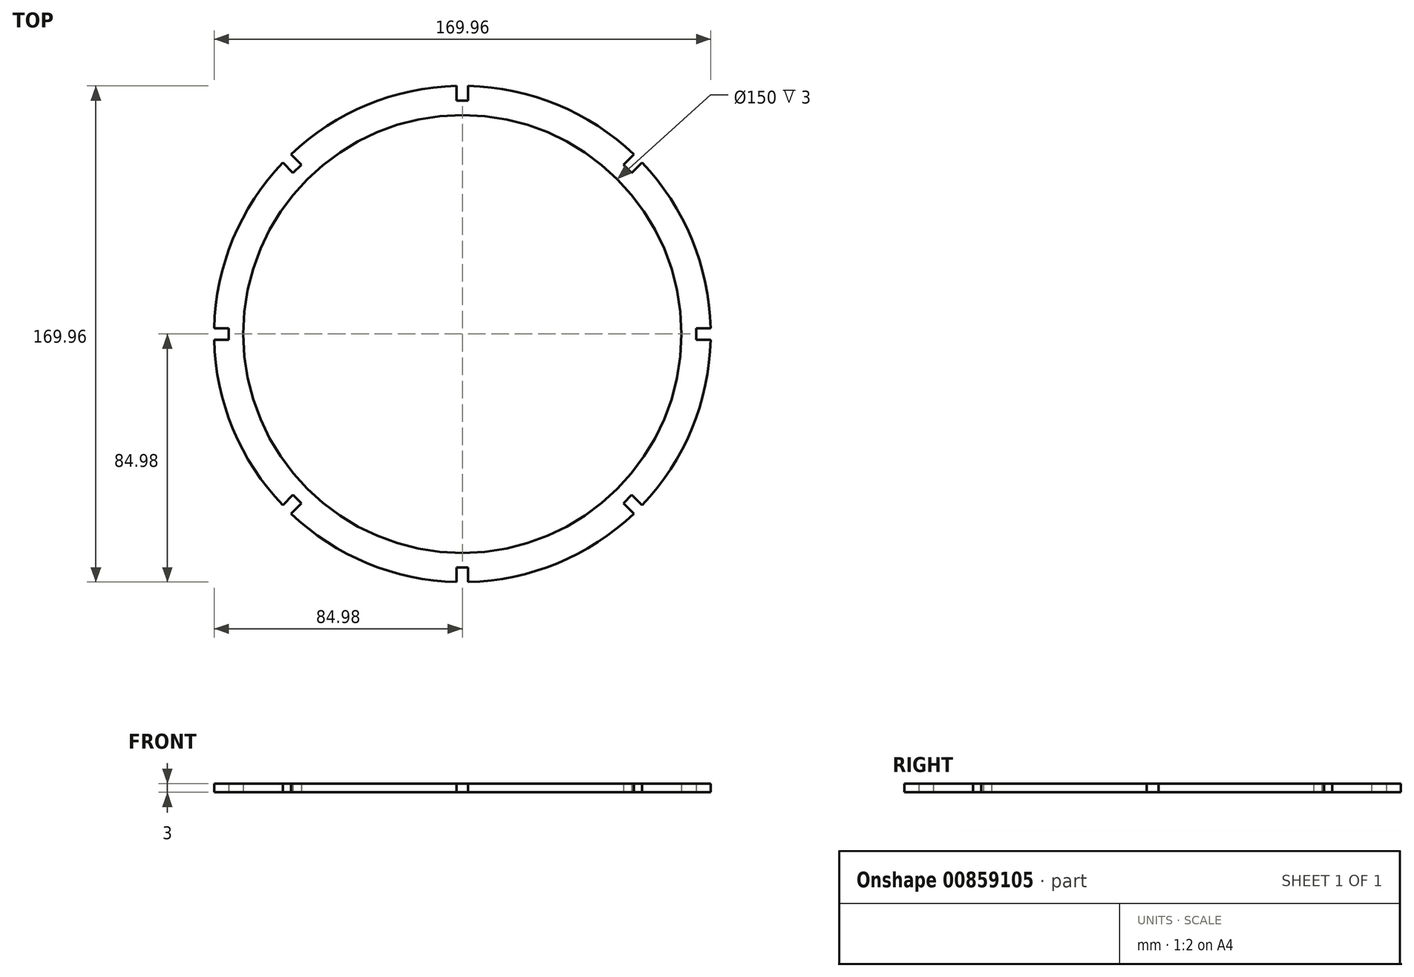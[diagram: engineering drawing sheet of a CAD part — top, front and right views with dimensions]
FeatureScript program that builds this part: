
annotation { "Feature Type Name" : "Feature", "Feature Type Description" : "" }
export const myFeature = defineFeature(function(context is Context, id is Id, definition is map)
    precondition{}
    {
        {
            var Q0;
            Q0=qCreatedBy(makeId("Top.planeOp"),FACE);
            var sketch = newSketch(context, id + "F0", { "sketchPlane" : qUnion([Q0])});
            skCircle(sketch, "E0", {"center": v(0, 0) * mm, "radius": 85 * mm});
            skCircle(sketch, "E1", {"center": v(0, 0) * mm, "radius": 75 * mm});
            skLineSegment(sketch, "E2", {"start": v(0, -79.98) * mm, "end": v(-2, -79.98) * mm});
            skLineSegment(sketch, "E3", {"start": v(-2, -79.98) * mm, "end": v(-2, -84.98) * mm});
            skLineSegment(sketch, "E4", {"start": v(-2, -84.98) * mm, "end": v(-2, -79.98) * mm});
            skLineSegment(sketch, "E5", {"start": v(0, -79.98) * mm, "end": v(2, -79.98) * mm});
            skLineSegment(sketch, "E6", {"start": v(2, -79.98) * mm, "end": v(2, -84.98) * mm});
            skLineSegment(sketch, "E7.1.0", {"start": v(55.14, -57.97) * mm, "end": v(58.67, -61.5) * mm});
            skLineSegment(sketch, "E7.1.1", {"start": v(56.55, -56.55) * mm, "end": v(55.14, -57.97) * mm});
            skLineSegment(sketch, "E7.1.2", {"start": v(56.55, -56.55) * mm, "end": v(57.97, -55.14) * mm});
            skLineSegment(sketch, "E7.1.3", {"start": v(57.97, -55.14) * mm, "end": v(61.5, -58.67) * mm});
            skLineSegment(sketch, "E7.2.0", {"start": v(79.98, -2) * mm, "end": v(84.98, -2) * mm});
            skLineSegment(sketch, "E7.2.1", {"start": v(79.98, 0) * mm, "end": v(79.98, -2) * mm});
            skLineSegment(sketch, "E7.2.2", {"start": v(79.98, 0) * mm, "end": v(79.98, 2) * mm});
            skLineSegment(sketch, "E7.2.3", {"start": v(79.98, 2) * mm, "end": v(84.98, 2) * mm});
            skLineSegment(sketch, "E7.3.0", {"start": v(57.97, 55.14) * mm, "end": v(61.5, 58.67) * mm});
            skLineSegment(sketch, "E7.3.1", {"start": v(56.55, 56.55) * mm, "end": v(57.97, 55.14) * mm});
            skLineSegment(sketch, "E7.3.2", {"start": v(56.55, 56.55) * mm, "end": v(55.14, 57.97) * mm});
            skLineSegment(sketch, "E7.3.3", {"start": v(55.14, 57.97) * mm, "end": v(58.67, 61.5) * mm});
            skLineSegment(sketch, "E7.4.0", {"start": v(2, 79.98) * mm, "end": v(2, 84.98) * mm});
            skLineSegment(sketch, "E7.4.1", {"start": v(0, 79.98) * mm, "end": v(2, 79.98) * mm});
            skLineSegment(sketch, "E7.4.2", {"start": v(0, 79.98) * mm, "end": v(-2, 79.98) * mm});
            skLineSegment(sketch, "E7.4.3", {"start": v(-2, 79.98) * mm, "end": v(-2, 84.98) * mm});
            skLineSegment(sketch, "E7.5.0", {"start": v(-55.14, 57.97) * mm, "end": v(-58.67, 61.5) * mm});
            skLineSegment(sketch, "E7.5.1", {"start": v(-56.55, 56.55) * mm, "end": v(-55.14, 57.97) * mm});
            skLineSegment(sketch, "E7.5.2", {"start": v(-56.55, 56.55) * mm, "end": v(-57.97, 55.14) * mm});
            skLineSegment(sketch, "E7.5.3", {"start": v(-57.97, 55.14) * mm, "end": v(-61.5, 58.67) * mm});
            skLineSegment(sketch, "E7.6.0", {"start": v(-79.98, 2) * mm, "end": v(-84.98, 2) * mm});
            skLineSegment(sketch, "E7.6.1", {"start": v(-79.98, 0) * mm, "end": v(-79.98, 2) * mm});
            skLineSegment(sketch, "E7.6.2", {"start": v(-79.98, 0) * mm, "end": v(-79.98, -2) * mm});
            skLineSegment(sketch, "E7.6.3", {"start": v(-79.98, -2) * mm, "end": v(-84.98, -2) * mm});
            skLineSegment(sketch, "E7.7.0", {"start": v(-57.97, -55.14) * mm, "end": v(-61.5, -58.67) * mm});
            skLineSegment(sketch, "E7.7.1", {"start": v(-56.55, -56.55) * mm, "end": v(-57.97, -55.14) * mm});
            skLineSegment(sketch, "E7.7.2", {"start": v(-56.55, -56.55) * mm, "end": v(-55.14, -57.97) * mm});
            skLineSegment(sketch, "E7.7.3", {"start": v(-55.14, -57.97) * mm, "end": v(-58.67, -61.5) * mm});
            skSolve(sketch);
        }
        {
            var Q0;
            Q0=makeQuery(id+"F0.imprint","IMPRINT",FACE,{"disambiguationData":[TD([[makeQuery(id+"F0.imprint","IMPRINT",EDGE,{"derivedFrom":sQuery(id+"F0.wireOp",EDGE,"E1")}),-1.0]])]});
            extrude(context, id + "F1", {"entities" : qUnion([Q0]), "depth" : 3 * mm, "offsetDistance" : 25 * mm});
        }
    });
